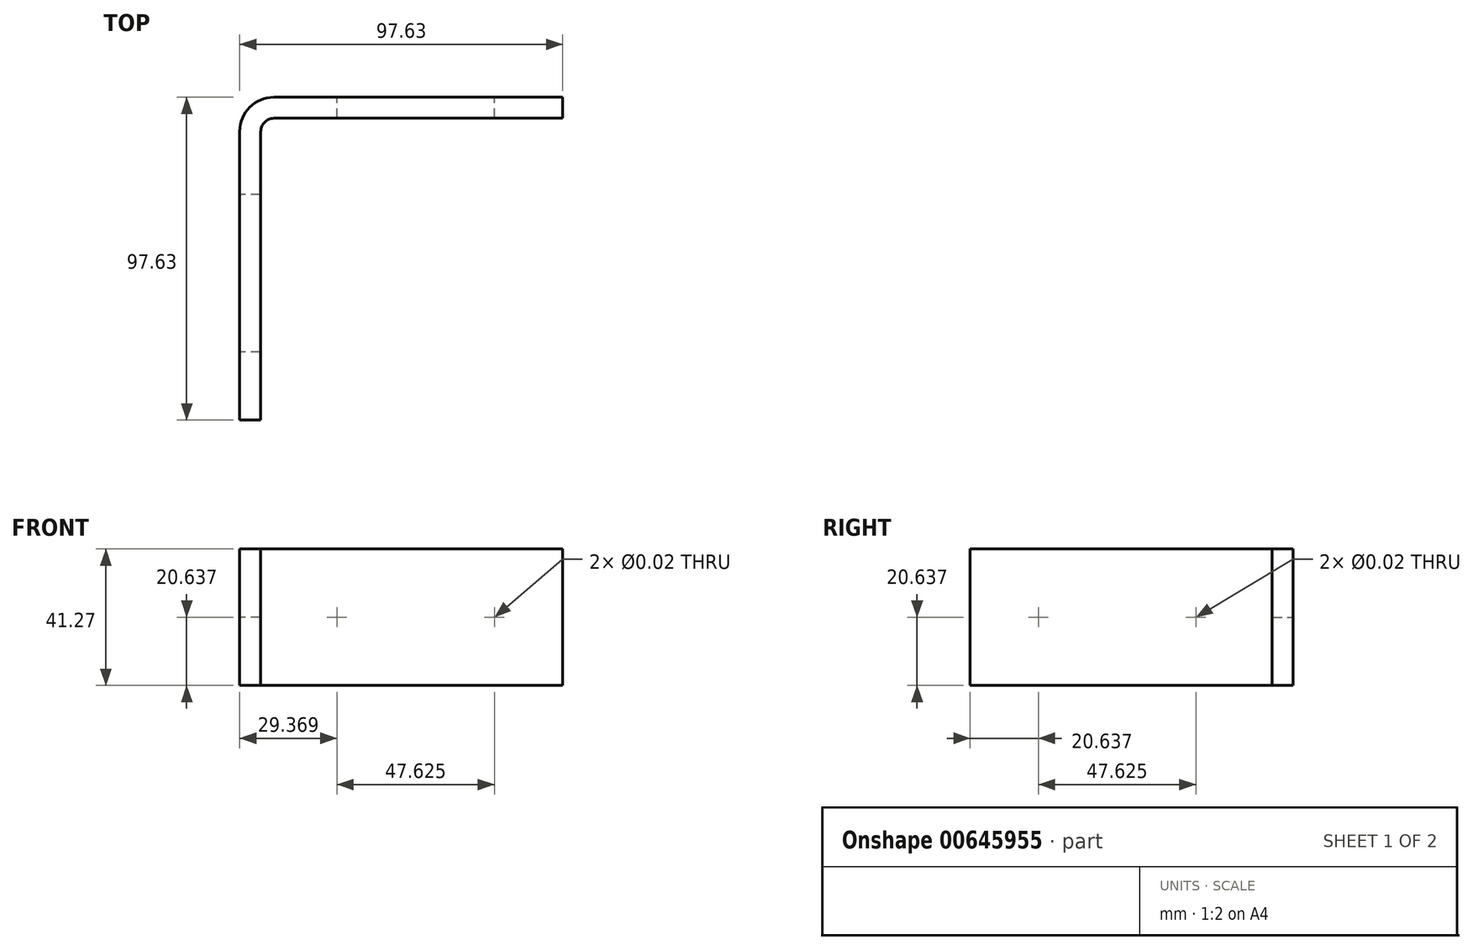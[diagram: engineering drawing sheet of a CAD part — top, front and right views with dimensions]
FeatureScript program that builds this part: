
annotation { "Feature Type Name" : "Feature", "Feature Type Description" : "" }
export const myFeature = defineFeature(function(context is Context, id is Id, definition is map)
    precondition{}
    {
        {
            var Q0;
            Q0=qCreatedBy(makeId("Top.planeOp"),FACE);
            var sketch = newSketch(context, id + "F0", { "sketchPlane" : qUnion([Q0])});
            skLineSegment(sketch, "E0", {"start": v(0, 87.31) * mm, "end": v(0, 0) * mm});
            skLineSegment(sketch, "E1", {"start": v(0, 0) * mm, "end": v(6.35, 0) * mm});
            skArc(sketch, "E2", {"start": v(10.32, 97.63) * mm, "mid": v(3.02, 94.6) * mm, "end": v(0, 87.31) * mm});
            skLineSegment(sketch, "E3", {"start": v(10.32, 97.63) * mm, "end": v(97.63, 97.63) * mm});
            skLineSegment(sketch, "E4", {"start": v(97.63, 91.28) * mm, "end": v(10.32, 91.28) * mm});
            skArc(sketch, "E5", {"start": v(10.32, 91.28) * mm, "mid": v(7.51, 90.12) * mm, "end": v(6.35, 87.31) * mm});
            skLineSegment(sketch, "E6", {"start": v(97.63, 97.63) * mm, "end": v(97.63, 91.28) * mm});
            skLineSegment(sketch, "E7", {"start": v(6.35, 0) * mm, "end": v(6.35, 87.31) * mm});
            skSolve(sketch);
        }
        {
            var Q0;
            Q0=makeQuery(id+"F0.imprint","IMPRINT",FACE,{"disambiguationData":[TD([[makeQuery(id+"F0.imprint","IMPRINT",EDGE,{"derivedFrom":sQuery(id+"F0.wireOp",EDGE,"E0")}),1.0]])]});
            extrude(context, id + "F1", {"entities" : qUnion([Q0]), "depth" : 41.27 * mm, "offsetDistance" : 25.4 * mm});
        }
        {
            var Q0;
            Q0=makeQuery(id+"F1.opExtrude","SWEPT_FACE",FACE,{"disambiguationData":[OSD([sQuery(id+"F0.wireOp",EDGE,"E7")])]});
            cPlane(context, id + "F2", {"entities" : qUnion([Q0]), "cplaneType" : CPlaneType.OFFSET, "offset" : 0 * mm, "width" : 152.4 * mm, "height" : 152.4 * mm});
        }
        {
            var Q0;
            Q0=qCreatedBy(id+"F2.planeOp",FACE);
            var sketch = newSketch(context, id + "F3", { "sketchPlane" : qUnion([Q0])});
            skPoint(sketch, "E8", {"position": v(20.64, 20.64) * mm});
            skPoint(sketch, "E9", {"position": v(68.26, 20.64) * mm});
            skSolve(sketch);
        }
        {
            var Q0;
            Q0=sQuery(id+"F3.wireOp",VERTEX,"E8");
            var Q1;
            Q1=sQuery(id+"F3.wireOp",VERTEX,"E9");
            var Q2;
            Q2=makeQuery(id+"F1.opExtrude","SWEPT_BODY",BODY,{"disambiguationData":[OSD([sQuery(id+"F0.wireOp",EDGE,"E0"),sQuery(id+"F0.wireOp",EDGE,"E1"),sQuery(id+"F0.wireOp",EDGE,"E2"),sQuery(id+"F0.wireOp",EDGE,"E3"),sQuery(id+"F0.wireOp",EDGE,"E4"),sQuery(id+"F0.wireOp",EDGE,"E5"),sQuery(id+"F0.wireOp",EDGE,"E6"),sQuery(id+"F0.wireOp",EDGE,"E7")])]});
            hole(context, id + "F4", {"style" : HoleStyle.SIMPLE, "endStyle" : HoleEndStyle.THROUGH, "standardTappedOrClearance" : lookupTablePath({ "standard" : "ANSI", "size" : "9/16 (0.56)", "type" : "Drilled" }), "standardBlindInLast" : lookupTablePath({ "standard" : "ANSI", "size" : "9/16 (0.56)", "type" : "Drilled" }), "holeDiameter" : 9 / 406.4 * mm, "majorDiameter" : 6.35 * mm, "tappedDepth" : 12.7 * mm, "tapClearance" : 3, "locations" : qUnion([Q0, Q1]), "scope" : qUnion([Q2]), "startStyle" : HoleStartStyle.PART});
        }
        {
            var Q0;
            Q0=makeQuery(id+"F1.opExtrude","SWEPT_FACE",FACE,{"disambiguationData":[OSD([sQuery(id+"F0.wireOp",EDGE,"E4")])]});
            cPlane(context, id + "F5", {"entities" : qUnion([Q0]), "cplaneType" : CPlaneType.OFFSET, "offset" : 0 * mm, "width" : 152.4 * mm, "height" : 152.4 * mm});
        }
        {
            var Q0;
            Q0=qCreatedBy(id+"F5.planeOp",FACE);
            var sketch = newSketch(context, id + "F6", { "sketchPlane" : qUnion([Q0])});
            skPoint(sketch, "E10", {"position": v(29.37, 20.64) * mm});
            skPoint(sketch, "E11", {"position": v(77, 20.64) * mm});
            skSolve(sketch);
        }
        {
            var Q0;
            Q0=sQuery(id+"F6.wireOp",VERTEX,"E10");
            var Q1;
            Q1=sQuery(id+"F6.wireOp",VERTEX,"E11");
            var Q2;
            Q2=makeQuery(id+"F1.opExtrude","SWEPT_BODY",BODY,{"disambiguationData":[OSD([sQuery(id+"F0.wireOp",EDGE,"E0"),sQuery(id+"F0.wireOp",EDGE,"E1"),sQuery(id+"F0.wireOp",EDGE,"E2"),sQuery(id+"F0.wireOp",EDGE,"E3"),sQuery(id+"F0.wireOp",EDGE,"E4"),sQuery(id+"F0.wireOp",EDGE,"E5"),sQuery(id+"F0.wireOp",EDGE,"E6"),sQuery(id+"F0.wireOp",EDGE,"E7")])]});
            hole(context, id + "F7", {"style" : HoleStyle.SIMPLE, "endStyle" : HoleEndStyle.THROUGH, "standardTappedOrClearance" : lookupTablePath({ "standard" : "ANSI", "size" : "9/16 (0.56)", "type" : "Drilled" }), "standardBlindInLast" : lookupTablePath({ "standard" : "ANSI", "size" : "9/16 (0.56)", "type" : "Drilled" }), "holeDiameter" : 9 / 406.4 * mm, "majorDiameter" : 6.35 * mm, "tappedDepth" : 12.7 * mm, "tapClearance" : 3, "locations" : qUnion([Q0, Q1]), "scope" : qUnion([Q2]), "startStyle" : HoleStartStyle.PART});
        }
    });
